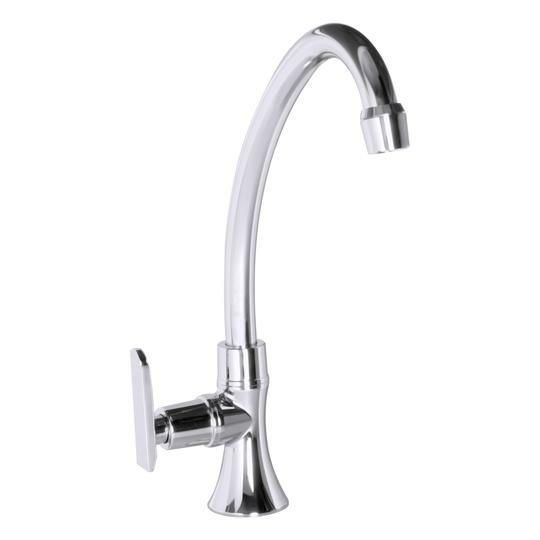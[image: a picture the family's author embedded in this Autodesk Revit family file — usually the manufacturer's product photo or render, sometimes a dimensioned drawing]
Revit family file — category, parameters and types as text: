
# Revit family: 01-1550-11 LLAVE MOVIL MESA LAVAPLATOS CISNE PIANA
name_source: partatom
category: Plumbing Fixtures
revit_build: Autodesk Revit 2018 (Build: 20170223_1515(x64)
units: mm (PartAtom-declared; Revit-internal decimal feet)

## family parameters
Cut with Voids When Loaded = No
Host = Face
OmniClass Number = 23.31.11.00
Part Type = Normal
Room Calculation Point = No
Round Connector Dimension = Use Diameter
Shared = No

## types (1)
- 01-1550-11
    Alto Aireador = 240 mm  [stored 0.787402 ft]
    Alto brazo = 304 mm  [stored 0.997375 ft]
    Alto manija = 75 mm  [stored 0.246063 ft]
    Ancho a manija = 74 mm
    Ancho brazo = 162 mm  [stored 0.531496 ft]
    Base = 50 mm
    CW Connection = Yes
    Default Elevation = 0 mm  [stored 0 ft]
    Description = Monomando
    HW Connection = Yes
    Link Ficha Tecnica = http://infotecnica.gricol.com
    Manufacturer = Gricol
    Model = 01-1550-11
    Plástico - ABS Cromado = Plastico ABS Cromado
    Product Name = LLAVE MOVIL MESA LAVAPLATOS CISNE PIANA
    Type Image = LLAVE MOVIL MESA LAVAPLATOS CISNE PIANA.jpg
    URL = https://www.gricol.com
    Vent Connection = No
    Waste Connection = No

note: [stored X ft] marks values corroborated as IEEE doubles in the binary element streams (Revit-internal decimal feet)

## geometry (parser evidence)
native form markers: Blend x2, Sweep x8
no freeform markers — native parametric forms only
